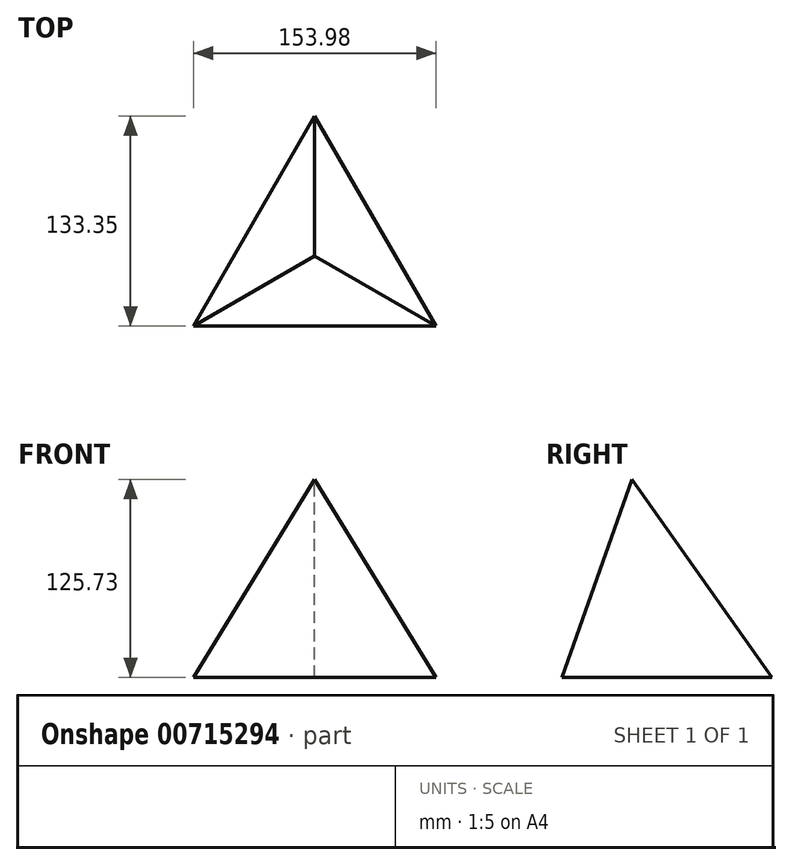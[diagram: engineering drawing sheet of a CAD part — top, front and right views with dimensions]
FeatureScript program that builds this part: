
annotation { "Feature Type Name" : "Feature", "Feature Type Description" : "" }
export const myFeature = defineFeature(function(context is Context, id is Id, definition is map)
    precondition{}
    {
        {
            var Q0;
            Q0=qCreatedBy(makeId("Top.planeOp"),FACE);
            var sketch = newSketch(context, id + "F0", { "sketchPlane" : qUnion([Q0])});
            skCircle(sketch, "E0", {"center": v(0, 0) * mm, "radius": 63.5 * mm, "construction": true});
            skLineSegment(sketch, "E1", {"start": v(0, 63.5) * mm, "end": v(-55, -31.75) * mm, "construction": true});
            skLineSegment(sketch, "E2", {"start": v(-55, -31.75) * mm, "end": v(55, -31.75) * mm, "construction": true});
            skLineSegment(sketch, "E3", {"start": v(55, -31.75) * mm, "end": v(0, 63.5) * mm, "construction": true});
            skLineSegment(sketch, "E4.0", {"start": v(0, 88.9) * mm, "end": v(-76.99, -44.45) * mm});
            skLineSegment(sketch, "E4.1", {"start": v(76.99, -44.45) * mm, "end": v(0, 88.9) * mm});
            skLineSegment(sketch, "E4.2", {"start": v(-76.99, -44.45) * mm, "end": v(76.99, -44.45) * mm});
            skSolve(sketch);
        }
        {
            var Q0;
            Q0=qCreatedBy(makeId("Top.planeOp"),FACE);
            cPlane(context, id + "F1", {"entities" : qUnion([Q0]), "cplaneType" : CPlaneType.OFFSET, "offset" : 125.73 * mm, "width" : 152.4 * mm, "height" : 152.4 * mm});
        }
        {
            var Q0;
            Q0=qCreatedBy(id+"F1.planeOp",FACE);
            var sketch = newSketch(context, id + "F2", { "sketchPlane" : qUnion([Q0])});
            skPoint(sketch, "E5", {"position": v(0, 0) * mm});
            skSolve(sketch);
        }
        {
            var Q0;
            Q0=makeQuery(id+"F0.imprint","IMPRINT",FACE,{"disambiguationData":[TD([[makeQuery(id+"F0.imprint","IMPRINT",EDGE,{"derivedFrom":sQuery(id+"F0.wireOp",EDGE,"E4.0")}),1.0]])]});
            var Q1;
            Q1=sQuery(id+"F2.wireOp",VERTEX,"E5");
            loft(context, id + "F3", {"sheetProfilesArray" : [{ "sheetProfileEntities" : qUnion([Q0]) }, { "sheetProfileEntities" : qUnion([Q1]) }]});
        }
    });
